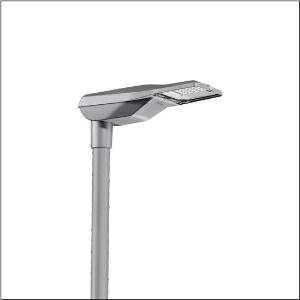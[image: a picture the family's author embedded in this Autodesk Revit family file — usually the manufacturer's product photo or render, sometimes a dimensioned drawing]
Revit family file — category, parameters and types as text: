
# Revit family: streetlight_sl_21_iq_micro___stw1_0a_5xe1e41d08cb_a1a9
name_source: partatom
category: Lighting Fixtures
units: mm (PartAtom-declared; Revit-internal decimal feet)

## family parameters
Cut with Voids When Loaded = No
Host = Face
Light Source = No
Part Type = Normal
Room Calculation Point = No
Round Connector Dimension = Use Diameter
Shared = No

## types (1)
- --- (1 x LED, 2980 lm, 19.4 W, 4000K)
    Apparent Load = 19 VA
    CIE Flux Codes = 38 75 98 100 100
    Color Rendering = 70
    Color Temperature = 4000K
    Default Elevation = 1800 mm
    Description = Streetlight SL 21 iQ micro, mast luminaire, primary light control with lens, of PMMA, primary optical cover: cover, of toughened safety glass, transparent, light distribution: STW1.0a, light emission: direct distribution, primary light characteristic: asymmetric, installation type: post-top, side-entry, LED, High Power LED, rated luminous flux: 2.980lm, luminous efficacy: 154lm/W, light colour: 740, colour temperature: 4000K, control: Auto-Match, Temp-Guard, Lumen-Switch, Night-Set, Smart-Wire, Light-Fading, Desk-Remote (wireless, voltage-free reading and setting of iQ features in the workshop via application-optimized NFC function/RFID function), optimised constant luminous flux control (CLO 2.0), presetting dimming linear, mains connection: 220..240V, AC, 50/60Hz, start of lifetime: 19W, end of service life: 20W, reduction: 10W, luminaire housing, of diecast aluminium, powder-coated, Siteco® metallic grey (DB 702S), corrosivity category C5 mid according to DIN EN ISO 12944, please order mast flange separately, inclination adjustable: 0°, 5°, 10°, 15°, sealing non-destructively replaceable, multi-level sealing system, length: 528mm, width: 235mm, height: 110mm, mast flange for spigot size: 42mm (side-entry): 5XC10008XM4, 60/48mm (side-entry/post-top): 5XC10108XM2, 76/60mm (side-entry/post-top): 5XC10108XM1, protection rating (complete): IP66, insulation class (complete): insulation class II (safety insulation), certification: CE, ENEC, ENEC+, VDE, impact resistance: IK09, permissible operating ambient temperature for outdoor applications: -40..+50°C, standard-compliant lighting for roads and squares, packaging unit: 1 piece

Light Distribution: STW1.0a
    Height = 110 mm
    Lamp = 1 x LED
    Lamp Light Flux = 2980 lm
    Lamp Power = 19.4 W
    Lamp count = 1
    Length = 528 mm
    Luminous efficacy = 154 lm/W
    Manufacturer = Siteco
    ModVariant = No
    Model = 5XE1E41D08CB
    Number of Poles = 1
    OnlyDefault = Yes
    Power Factor = 1
    Product Name = Streetlight SL 21 iQ micro | STW1.0a
    Product group = mast luminaire | pylon top
    ProductGroupID = 6100
    Protection Class = Protection class II
    Protection Degree = IP 66
    RLX_Detail_Level = 1
    RLX_Emergency_Light_Flux = 0 lm
    RLX_Emergency_Type = 0
    RLX_Emergency_Type_DB = No
    RlxData = <blob elided: 98669 chars, md5=2af38486>
    Socket = socket
    Standby Power = 0 W
    System Light Flux = 2980 lm
    System Power = 19 W
    Type Comments = factory setting: luminous flux: 100 % | dim-lin: 254 | 387 mA
    Type Image = l_1006881.jpg
    URL = http://relux.com
    VarID = @adj_070149
    Voltage = 0 V
    Weight = 0.00 kg
    Width = 235 mm

## geometry (parser evidence)
native form markers: Blend x4, Sweep x9
no freeform markers — native parametric forms only
